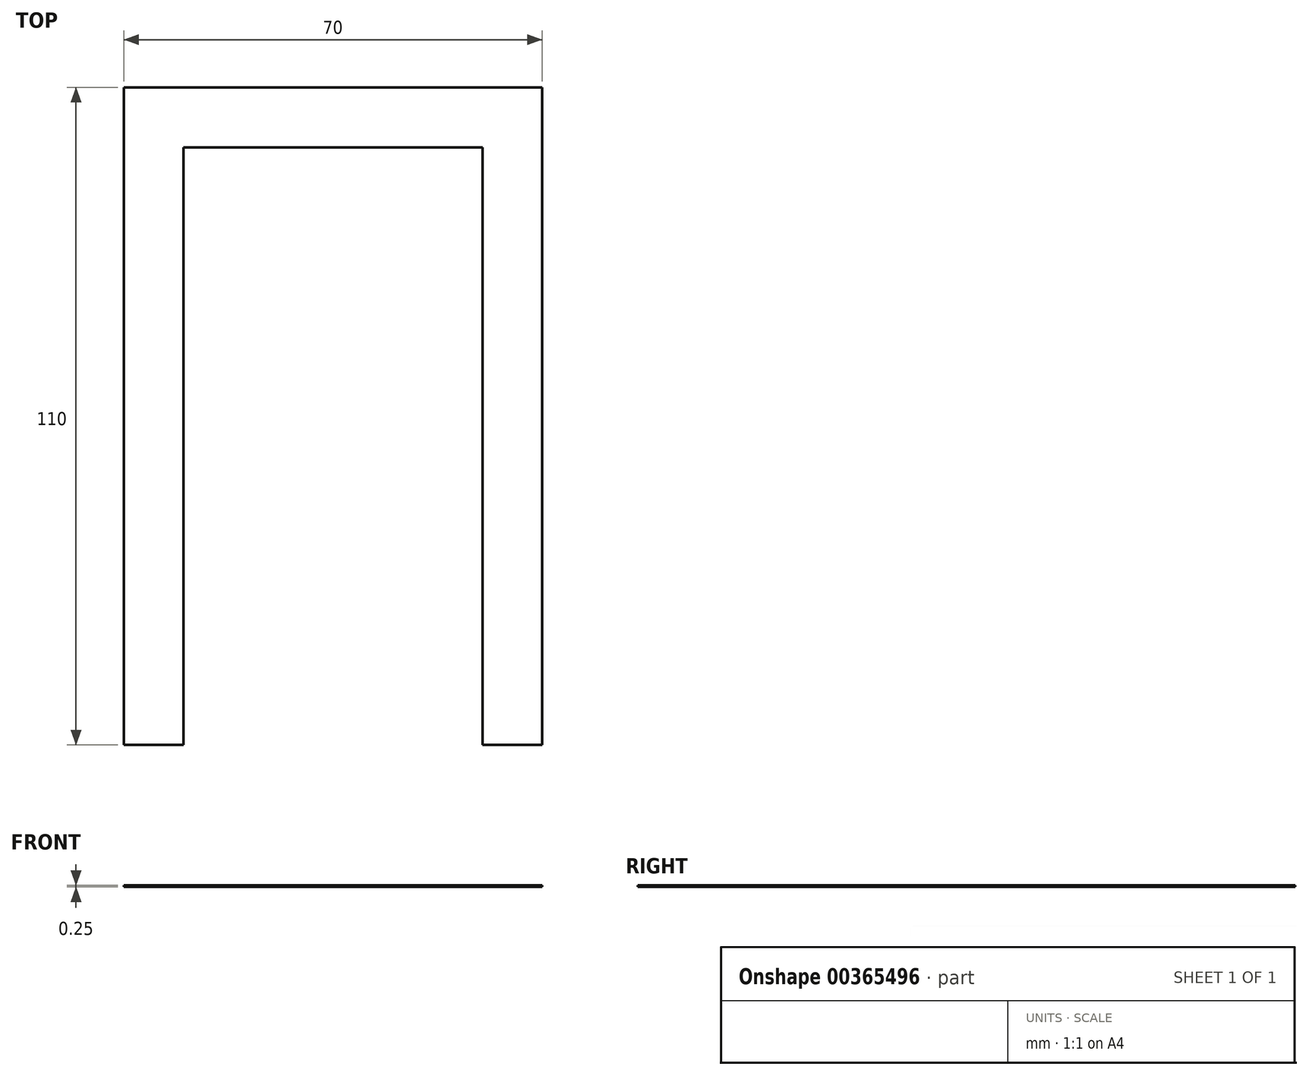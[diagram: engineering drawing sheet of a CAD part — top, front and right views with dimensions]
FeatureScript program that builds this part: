
annotation { "Feature Type Name" : "Feature", "Feature Type Description" : "" }
export const myFeature = defineFeature(function(context is Context, id is Id, definition is map)
    precondition{}
    {
        {
            var Q0;
            Q0=qCreatedBy(makeId("Top.planeOp"),FACE);
            var sketch = newSketch(context, id + "F0", { "sketchPlane" : qUnion([Q0])});
            skLineSegment(sketch, "E0", {"start": v(-35, 10) * mm, "end": v(35, 10) * mm});
            skLineSegment(sketch, "E1", {"start": v(35, 10) * mm, "end": v(35, -100) * mm});
            skLineSegment(sketch, "E2", {"start": v(35, -100) * mm, "end": v(25, -100) * mm});
            skLineSegment(sketch, "E3", {"start": v(25, -100) * mm, "end": v(25, 0) * mm});
            skLineSegment(sketch, "E4", {"start": v(25, 0) * mm, "end": v(-25, 0) * mm});
            skLineSegment(sketch, "E5", {"start": v(-25, 0) * mm, "end": v(-25, -100) * mm});
            skLineSegment(sketch, "E6", {"start": v(-25, -100) * mm, "end": v(-35, -100) * mm});
            skLineSegment(sketch, "E7", {"start": v(-35, -100) * mm, "end": v(-35, 10) * mm});
            skSolve(sketch);
        }
        {
            var Q0;
            Q0 = qSketchRegion(id + "F0", true);
            extrude(context, id + "F1", {"entities" : qUnion([Q0]), "depth" : 0.25 * mm});
        }
    });
